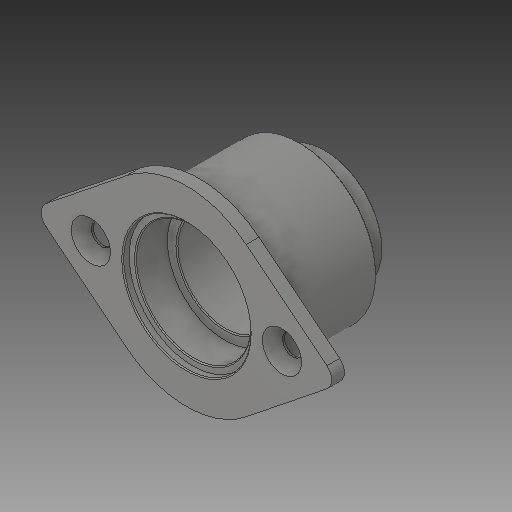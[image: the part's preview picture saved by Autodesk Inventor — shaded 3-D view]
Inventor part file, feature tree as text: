
AUTODESK INVENTOR PART (.ipt)
format: ipt  version: 2017 (Build 210142000, 142)  size: 178,688 bytes
history: native  units: in
note: dims shown in document units (in); Inventor stores cm internally (conversion verified against a paired STEP export)
features: chamfer x1
ambient origin geometry x8: Origin, YZ Plane, XZ Plane, XY Plane, X Axis, Y Axis, Z Axis, Center Point
bodies: Solid1 (feature_tree)
feature tree (1):
  chamfer  "Chamfer1"  [1 undecoded]
note: 1 required parameter value undecoded (feature->parameter linkage not recoverable at this tier; creation-order binding heuristic only, values carry confidence <= 0.55)
